# Revit family: 0049284+0049342
name_source: partatom
category: Lighting Fixtures
revit_build: Autodesk Revit 2017 (Build: 20190507_1515(x64)
units: mm (PartAtom-declared; Revit-internal decimal feet)

## family parameters
Cut with Voids When Loaded = No
Host = Face
Light Source = Yes
OmniClass Number = 23.80.70.00
OmniClass Title = Lighting
Part Type = Normal
Room Calculation Point = No
Round Connector Dimension = Use Diameter
Shared = No

## types (2) — shared parameters
Apparent Load = 12 VA
Assembly Code = D5020200
AssetType = Fixed
ClassificationName = Uniclass2015
ClassificationValue = EF_70_80
Color Filter = 16777215
Default Elevation = 1219 mm
Description = LED exterior surface mounted luminaire, 1050lm, 12W power consumption, 88lm/W efficacy, 3000K color temperature, CRI80, non-dimmable, IP66, IK10, 50,000 hours (L70), black housing, vandal resistant
Dimming Lamp Color Temperature Shift = <None>
DocumentationLiterature = http://www.sylvania-lighting.com
DurationUnit = hours
ElectricShockClassification = Class II
Emit Shape Visible in Rendering = No
Emit from Circle Diameter = 200 mm  [stored 0.656168 ft]
ExpectedLife = 50000
HoleAngle_SYL = 45.00°
HoleHoleRad_SYL = 6 mm  [stored 0.019685 ft]
HoleRad_SYL = 134 mm
IfcExportAs = IfcLightFixtureType
IfcExportType = IfcLightFixtureType
ImpactProtectionIndex = IK10
IngressProtection = IP66
InputNominalFrequency = 50/60 Hz
InputVoltage = 220-240 V AC
Keynote = 16500
Lamp = LED
LampColourRenderingIndex = 80
LampColourTemperature = 3000 K
LampNominalLuminous = 1050 lm
LampsType = LED
LuminousEfficacy = 88 lm/W
Manufacturer = Feilo Sylvania
ManufacturerName = Feilo Sylvania
Material = pc polycarbonate housing, pc polycarbonate diffuser
Material_1_SYL = Body-Sylvania-StartSurfaceIP66-Black
Material_2_SYL = Diffuser-Sylvania-StartSurfaceIP66
Material_3_SYL = LED-Sylvania-StartSurfaceIP66
Model = START Surface IP66 1050lm 830 IK10 BLK
ModelNumber = 0049284
ModelReference = START Surface IP66 1050lm 830 IK10 BLK
Name = START Surface IP66 1050lm 830 IK10 BLK
NominalDepth = 300 mm
NominalHeight = 90 mm  [stored 0.295276 ft]
NominalLength = 300 mm
PowerConsumption = 12 W
Tilt Angle = -90.00°
Type Image = <None>
TypeName = START Surface IP66 1050lm 830 IK10 BLK
URL = http://www.sylvania-lighting.com
Voltage = 0 V
Weight = 4.68 kg
zero-valued in all types: Cost, PowerFactor

## per-type parameters (varying)
| type | Eyelid_SYL | Photometric Web File |
| 0049284 START Surface IP66 1050lm 830 BLK | No | 0049284.ies |
| 0049284+0049342 START Surface IP66 1050lm 830 BLK + Eyelid | Yes | 0049284+0049342.ies |

note: [stored X ft] marks values corroborated as IEEE doubles in the binary element streams (Revit-internal decimal feet)

## geometry (parser evidence)
native form markers: Sweep x3
no freeform markers — native parametric forms only
